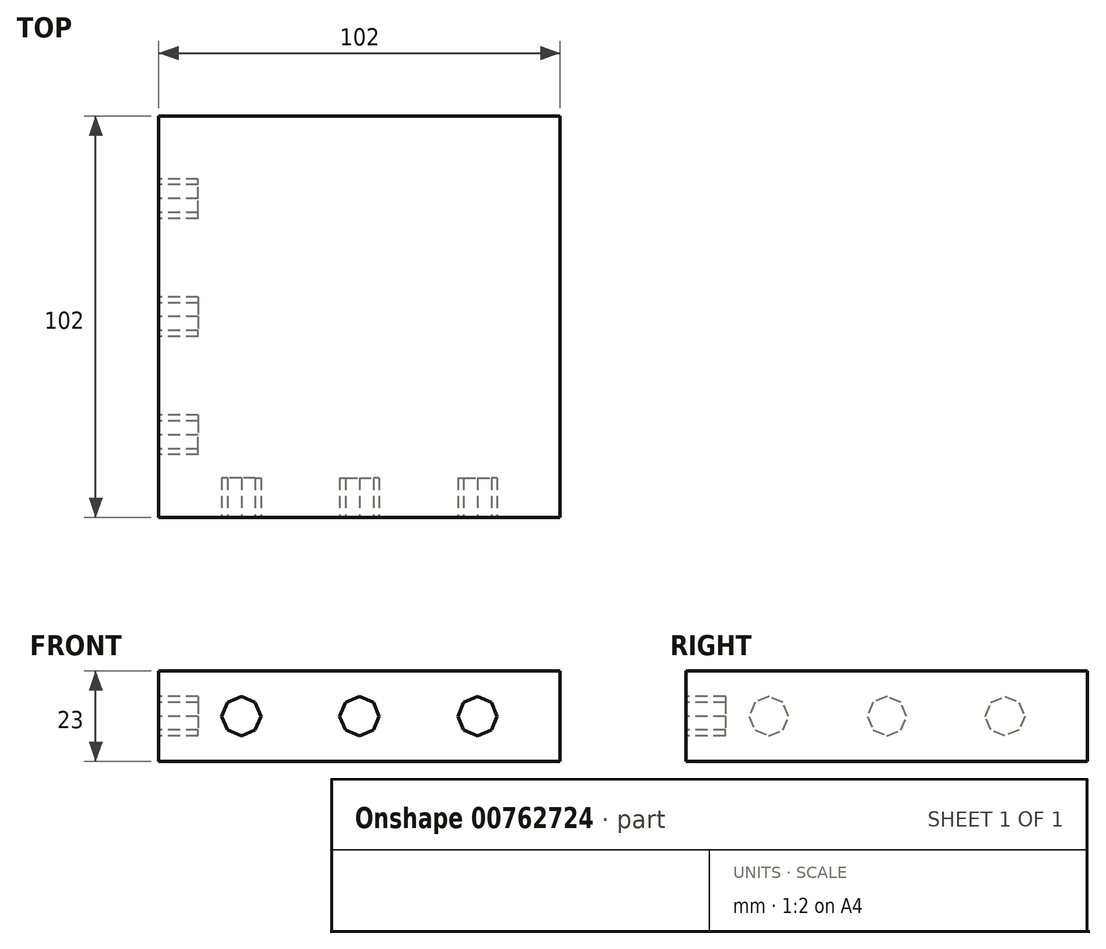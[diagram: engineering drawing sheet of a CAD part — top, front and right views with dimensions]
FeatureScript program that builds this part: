
annotation { "Feature Type Name" : "Feature", "Feature Type Description" : "" }
export const myFeature = defineFeature(function(context is Context, id is Id, definition is map)
    precondition{}
    {
        {
            var Q0;
            Q0=qCreatedBy(makeId("Right.planeOp"),FACE);
            var sketch = newSketch(context, id + "F0", { "sketchPlane" : qUnion([Q0])});
            skLineSegment(sketch, "E0.bottom", {"start": v(51, -11.5) * mm, "end": v(-51, -11.5) * mm});
            skLineSegment(sketch, "E0.top", {"start": v(51, 11.5) * mm, "end": v(-51, 11.5) * mm});
            skLineSegment(sketch, "E0.left", {"start": v(51, -11.5) * mm, "end": v(51, 11.5) * mm});
            skLineSegment(sketch, "E0.right", {"start": v(-51, -11.5) * mm, "end": v(-51, 11.5) * mm});
            skPoint(sketch, "E0.middle", {"position": v(0, 0) * mm});
            skSolve(sketch);
        }
        {
            var Q0;
            Q0 = qSketchRegion(id + "F0", true);
            extrude(context, id + "F1", {"entities" : qUnion([Q0]), "endBound" : BoundingType.SYMMETRIC, "depth" : 102 * mm, "offsetDistance" : 25 * mm});
        }
        {
            var Q0;
            Q0=makeQuery(id+"F1.opExtrude","SWEPT_FACE",FACE,{"disambiguationData":[OSD([sQuery(id+"F0.wireOp",EDGE,"E0.right")])]});
            var sketch = newSketch(context, id + "F2", { "sketchPlane" : qUnion([Q0])});
            skCircle(sketch, "E1", {"center": v(0, 0) * mm, "radius": 5 * mm, "construction": true});
            skLineSegment(sketch, "E2.0", {"start": v(5, 0) * mm, "end": v(3.54, -3.54) * mm});
            skLineSegment(sketch, "E2.1", {"start": v(3.54, -3.54) * mm, "end": v(0, -5) * mm});
            skLineSegment(sketch, "E2.2", {"start": v(0, -5) * mm, "end": v(-3.54, -3.54) * mm});
            skLineSegment(sketch, "E2.3", {"start": v(-3.54, -3.54) * mm, "end": v(-5, 0) * mm});
            skLineSegment(sketch, "E2.4", {"start": v(-5, 0) * mm, "end": v(-3.54, 3.54) * mm});
            skLineSegment(sketch, "E2.5", {"start": v(-3.54, 3.54) * mm, "end": v(0, 5) * mm});
            skLineSegment(sketch, "E2.6", {"start": v(0, 5) * mm, "end": v(3.54, 3.54) * mm});
            skLineSegment(sketch, "E2.7", {"start": v(3.54, 3.54) * mm, "end": v(5, 0) * mm});
            skLineSegment(sketch, "E3.1.0.0", {"start": v(30, 5) * mm, "end": v(33.54, 3.54) * mm});
            skLineSegment(sketch, "E3.1.0.1", {"start": v(26.46, 3.54) * mm, "end": v(30, 5) * mm});
            skLineSegment(sketch, "E3.1.0.2", {"start": v(25, 0) * mm, "end": v(26.46, 3.54) * mm});
            skLineSegment(sketch, "E3.1.0.3", {"start": v(26.46, -3.54) * mm, "end": v(25, 0) * mm});
            skLineSegment(sketch, "E3.1.0.4", {"start": v(30, -5) * mm, "end": v(26.46, -3.54) * mm});
            skLineSegment(sketch, "E3.1.0.5", {"start": v(33.54, -3.54) * mm, "end": v(30, -5) * mm});
            skLineSegment(sketch, "E3.1.0.6", {"start": v(35, 0) * mm, "end": v(33.54, -3.54) * mm});
            skLineSegment(sketch, "E3.1.0.7", {"start": v(33.54, 3.54) * mm, "end": v(35, 0) * mm});
            skLineSegment(sketch, "E3.direction1", {"start": v(0, 5) * mm, "end": v(30, 5) * mm, "construction": true});
            skLineSegment(sketch, "E4.MirrorCS", {"start": v(-30, 5) * mm, "end": v(-33.54, 3.54) * mm});
            skLineSegment(sketch, "E5.MirrorCS", {"start": v(-33.54, 3.54) * mm, "end": v(-35, 0) * mm});
            skLineSegment(sketch, "E6.MirrorCS", {"start": v(-35, 0) * mm, "end": v(-33.54, -3.54) * mm});
            skLineSegment(sketch, "E7.MirrorCS", {"start": v(-33.54, -3.54) * mm, "end": v(-30, -5) * mm});
            skLineSegment(sketch, "E8.MirrorCS", {"start": v(-30, -5) * mm, "end": v(-26.46, -3.54) * mm});
            skLineSegment(sketch, "E9.MirrorCS", {"start": v(-26.46, -3.54) * mm, "end": v(-25, 0) * mm});
            skLineSegment(sketch, "E10.MirrorCS", {"start": v(-26.46, 3.54) * mm, "end": v(-30, 5) * mm});
            skLineSegment(sketch, "E11.MirrorCS", {"start": v(-25, 0) * mm, "end": v(-26.46, 3.54) * mm});
            skSolve(sketch);
        }
        {
            var Q0;
            Q0 = qSketchRegion(id + "F2", true);
            extrude(context, id + "F3", {"entities" : qUnion([Q0]), "operationType" : NewBodyOperationType.REMOVE, "oppositeDirection" : true, "depth" : 10 * mm, "offsetDistance" : 25 * mm});
        }
        {
            var Q0;
            Q0=makeQuery(id+"F1.opExtrude","CAP_FACE",FACE,{"disambiguationData":[OSD([sQuery(id+"F0.wireOp",EDGE,"E0.bottom"),sQuery(id+"F0.wireOp",EDGE,"E0.top"),sQuery(id+"F0.wireOp",EDGE,"E0.left"),sQuery(id+"F0.wireOp",EDGE,"E0.right")])],"isStart":true});
            var sketch = newSketch(context, id + "F4", { "sketchPlane" : qUnion([Q0])});
            skCircle(sketch, "E12.cCircle", {"center": v(0, 0) * mm, "radius": 5 * mm, "construction": true});
            skLineSegment(sketch, "E12.0", {"start": v(5, 0) * mm, "end": v(3.54, -3.54) * mm});
            skLineSegment(sketch, "E12.1", {"start": v(3.54, -3.54) * mm, "end": v(0, -5) * mm});
            skLineSegment(sketch, "E12.2", {"start": v(0, -5) * mm, "end": v(-3.54, -3.54) * mm});
            skLineSegment(sketch, "E12.3", {"start": v(-3.54, -3.54) * mm, "end": v(-5, 0) * mm});
            skLineSegment(sketch, "E12.4", {"start": v(-5, 0) * mm, "end": v(-3.54, 3.54) * mm});
            skLineSegment(sketch, "E12.5", {"start": v(-3.54, 3.54) * mm, "end": v(0, 5) * mm});
            skLineSegment(sketch, "E12.6", {"start": v(0, 5) * mm, "end": v(3.54, 3.54) * mm});
            skLineSegment(sketch, "E12.7", {"start": v(3.54, 3.54) * mm, "end": v(5, 0) * mm});
            skLineSegment(sketch, "E13.1.0.0", {"start": v(26.46, 3.54) * mm, "end": v(30, 5) * mm});
            skLineSegment(sketch, "E13.1.0.1", {"start": v(30, 5) * mm, "end": v(33.54, 3.54) * mm});
            skLineSegment(sketch, "E13.1.0.2", {"start": v(33.54, 3.54) * mm, "end": v(35, 0) * mm});
            skLineSegment(sketch, "E13.1.0.3", {"start": v(35, 0) * mm, "end": v(33.54, -3.54) * mm});
            skLineSegment(sketch, "E13.1.0.4", {"start": v(33.54, -3.54) * mm, "end": v(30, -5) * mm});
            skLineSegment(sketch, "E13.1.0.5", {"start": v(30, -5) * mm, "end": v(26.46, -3.54) * mm});
            skLineSegment(sketch, "E13.1.0.6", {"start": v(26.46, -3.54) * mm, "end": v(25, 0) * mm});
            skLineSegment(sketch, "E13.1.0.7", {"start": v(25, 0) * mm, "end": v(26.46, 3.54) * mm});
            skLineSegment(sketch, "E13.direction1", {"start": v(-3.54, 3.54) * mm, "end": v(26.46, 3.54) * mm, "construction": true});
            skLineSegment(sketch, "E14.MirrorCS", {"start": v(-26.46, 3.54) * mm, "end": v(-30, 5) * mm});
            skLineSegment(sketch, "E15.MirrorCS", {"start": v(-30, 5) * mm, "end": v(-33.54, 3.54) * mm});
            skLineSegment(sketch, "E16.MirrorCS", {"start": v(-33.54, 3.54) * mm, "end": v(-35, 0) * mm});
            skLineSegment(sketch, "E17.MirrorCS", {"start": v(-35, 0) * mm, "end": v(-33.54, -3.54) * mm});
            skLineSegment(sketch, "E18.MirrorCS", {"start": v(-33.54, -3.54) * mm, "end": v(-30, -5) * mm});
            skLineSegment(sketch, "E19.MirrorCS", {"start": v(-30, -5) * mm, "end": v(-26.46, -3.54) * mm});
            skLineSegment(sketch, "E20.MirrorCS", {"start": v(-26.46, -3.54) * mm, "end": v(-25, 0) * mm});
            skLineSegment(sketch, "E21.MirrorCS", {"start": v(-25, 0) * mm, "end": v(-26.46, 3.54) * mm});
            skSolve(sketch);
        }
        {
            var Q0;
            Q0 = qSketchRegion(id + "F4", true);
            extrude(context, id + "F5", {"entities" : qUnion([Q0]), "operationType" : NewBodyOperationType.REMOVE, "oppositeDirection" : true, "depth" : 10 * mm, "offsetDistance" : 25 * mm});
        }
        {
            var Q0;
            Q0=makeQuery(id+"F1.opExtrude","SWEPT_BODY",BODY,{"disambiguationData":[OSD([sQuery(id+"F0.wireOp",EDGE,"E0.bottom"),sQuery(id+"F0.wireOp",EDGE,"E0.top"),sQuery(id+"F0.wireOp",EDGE,"E0.left"),sQuery(id+"F0.wireOp",EDGE,"E0.right")])]});
            transform(context, id + "F6", {"entities" : qUnion([Q0]), "transformType" : TransformType.TRANSLATION_3D, "dx" : 0 * mm, "dy" : 0 * mm, "dz" : 0 * mm, "makeCopy" : true});
        }
        {
            var Q0;
            Q0=makeQuery(id+"F6.opPattern","COPY",BODY,{"derivedFrom":makeQuery(id+"F1.opExtrude","SWEPT_BODY",BODY,{"disambiguationData":[OSD([sQuery(id+"F0.wireOp",EDGE,"E0.bottom"),sQuery(id+"F0.wireOp",EDGE,"E0.top"),sQuery(id+"F0.wireOp",EDGE,"E0.left"),sQuery(id+"F0.wireOp",EDGE,"E0.right")])]}),"instanceName":"1"});
            deleteBodies(context, id + "F7", {"entities" : qUnion([Q0])});
        }
    });
